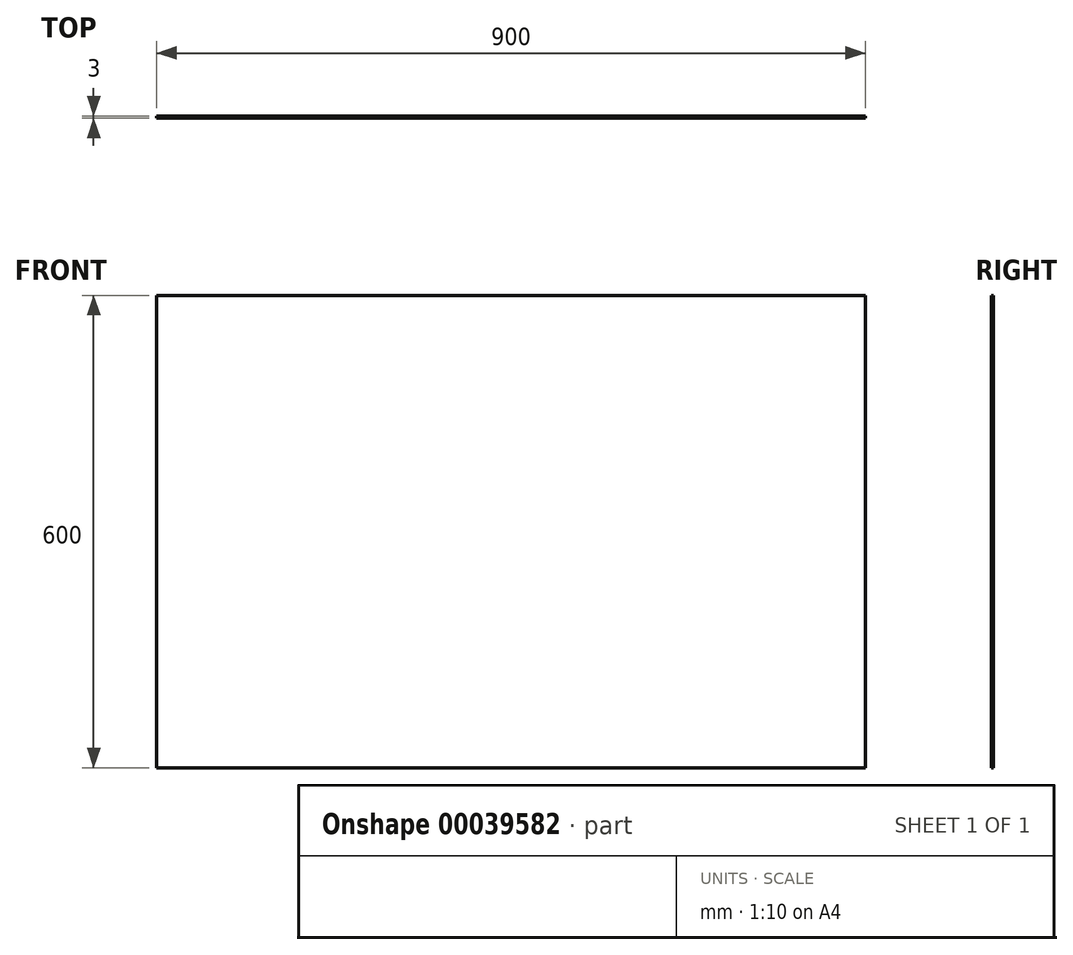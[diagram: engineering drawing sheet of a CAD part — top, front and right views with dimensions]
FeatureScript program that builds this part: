
annotation { "Feature Type Name" : "Feature", "Feature Type Description" : "" }
export const myFeature = defineFeature(function(context is Context, id is Id, definition is map)
    precondition{}
    {
        {
            var Q0;
            Q0=qCreatedBy(makeId("Front.planeOp"),FACE);
            var sketch = newSketch(context, id + "F0", { "sketchPlane" : qUnion([Q0])});
            skLineSegment(sketch, "E0.bottom", {"start": v(-1114.17, 423.11) * mm, "end": v(-214.17, 423.11) * mm});
            skLineSegment(sketch, "E0.top", {"start": v(-1114.17, -176.89) * mm, "end": v(-214.17, -176.89) * mm});
            skLineSegment(sketch, "E0.left", {"start": v(-1114.17, 423.11) * mm, "end": v(-1114.17, -176.89) * mm});
            skLineSegment(sketch, "E0.right", {"start": v(-214.17, 423.11) * mm, "end": v(-214.17, -176.89) * mm});
            skSolve(sketch);
        }
        {
            var Q0;
            Q0=makeQuery(id+"F0.imprint","IMPRINT",FACE,{"disambiguationData":[TD([[makeQuery(id+"F0.imprint","IMPRINT",EDGE,{"derivedFrom":sQuery(id+"F0.wireOp",EDGE,"E0.bottom")}),-1.0]])]});
            extrude(context, id + "F1", {"entities" : qUnion([Q0]), "depth" : 3 * mm});
        }
    });
